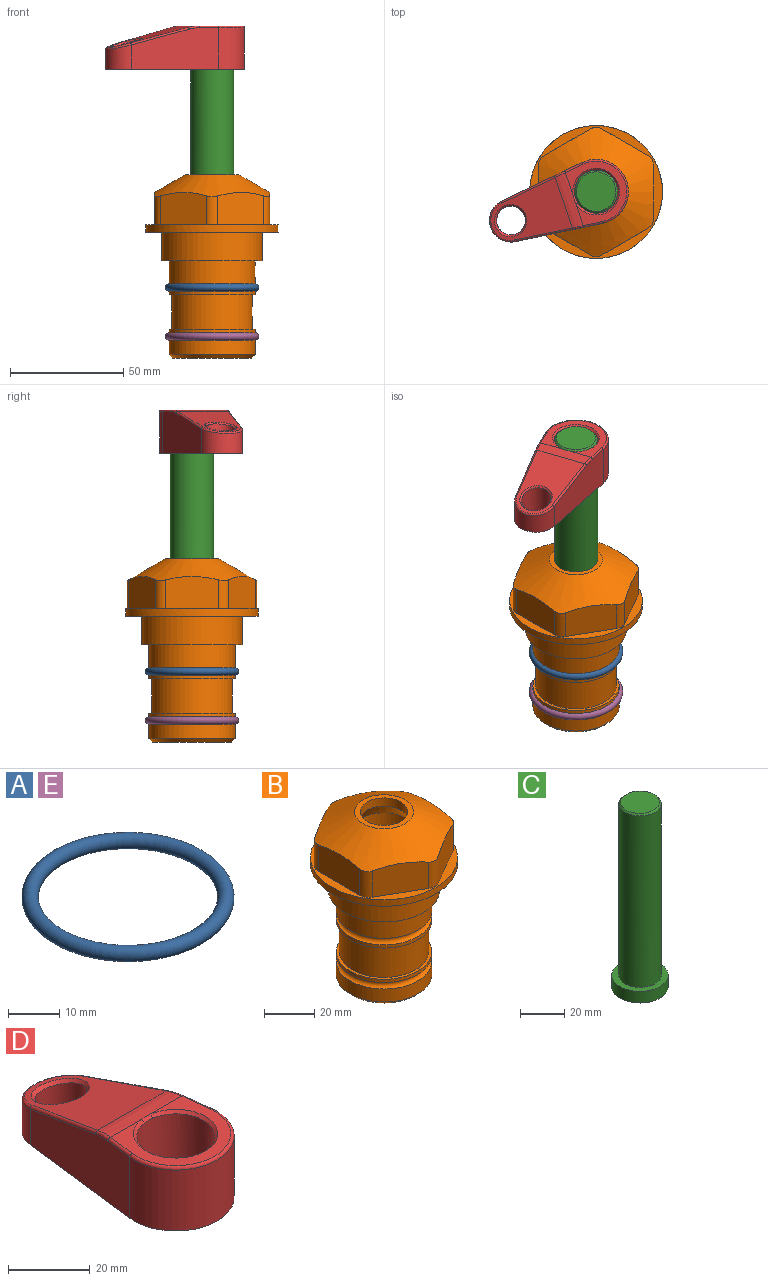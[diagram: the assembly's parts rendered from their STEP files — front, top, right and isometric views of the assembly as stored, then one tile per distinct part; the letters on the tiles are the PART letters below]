
ASSEMBLY  parts=5 mates=4
PART A: 1 faces, bbox 44.7x44.7x3.2 mm
  f0: torus R=19.05mm, axis (0,0,1), area 1193.9mm2
PART B: 36 faces, bbox 58.7x58.7x81 mm
  f0: cylinder r=17.78mm len=35.56mm, axis (0,0,1), area 1670.8mm2, adj f23,f24,f31
  f1: cylinder r=19.05mm len=38.1mm, axis (0,0,1), area 1191.9mm2, adj f26,f27,f30
  f2: plane 58.66x58.66mm, normal (0,0,-1), area 1150.6mm2, adj f3,f28
  f3: cylinder r=29.33mm len=58.66mm, axis (0,0,-1), area 585.1mm2, adj f2,f4
  f4: plane 58.66x58.66mm, normal (0,0,1), area 475.9mm2, adj f3,f5,f6,f7,f8,f9,f10,f11
  f5: plane 20.32x14.34mm, normal (-0.5,0.87,0), area 324.4mm2, adj f4,f15,f16,f17
  f6: plane 20.32x14.34mm, normal (0.5,0.87,0), area 324.4mm2, adj f4,f14,f15,f17
  f7: plane 23.48x14.34mm, normal (1,0,0), area 324.4mm2, adj f4,f13,f14,f17
  f8: plane 20.32x14.34mm, normal (0.5,-0.87,0), area 324.4mm2, adj f4,f12,f13,f17
  f9: plane 20.32x14.34mm, normal (-0.5,-0.87,0), area 324.4mm2, adj f4,f11,f12,f17
  f10: plane 23.48x14.34mm, normal (-1,0,0), area 324.4mm2, adj f4,f11,f16,f17
  f11: cylinder r=5.08mm len=12.85mm, axis (0,0,-1), area 67.2mm2, adj f4,f9,f10,f17
  f12: cylinder r=5.08mm len=12.85mm, axis (0,0,-1), area 67.2mm2, adj f4,f8,f9,f17
  f13: cylinder r=5.08mm len=12.85mm, axis (0,0,-1), area 67.2mm2, adj f4,f7,f8,f17
  f14: cylinder r=5.08mm len=12.85mm, axis (0,0,-1), area 67.2mm2, adj f4,f6,f7,f17
  f15: cylinder r=5.08mm len=12.85mm, axis (0,0,-1), area 67.2mm2, adj f4,f5,f6,f17
  f16: cylinder r=5.08mm len=12.85mm, axis (0,0,-1), area 67.2mm2, adj f4,f5,f10,f17
  f17: cone r=11.73mm half-angle=60deg, axis (0,0,-1), area 2071.8mm2, adj f5,f6,f7,f8,f9,f10,f11,f12
  f18: plane 23.46x23.46mm, normal (0,0,1), area 147.4mm2, adj f17,f35
  f19: plane 34.93x34.93mm, normal (0,0,-1), area 958mm2, adj f29
  f20: cylinder r=19.05mm len=38.1mm, axis (0,0,1), area 760.1mm2, adj f21,f29
  f21: torus R=19.05mm, axis (0,0,1), area 565.3mm2, adj f20,f22
  f22: cylinder r=19.05mm len=38.1mm, axis (0,0,1), area 190mm2, adj f21,f23
  f23: plane 38.1x38.1mm, normal (0,0,1), area 146.9mm2, adj f0,f22
  f24: plane 38.1x38.1mm, normal (0,0,-1), area 146.9mm2, adj f0,f25
  f25: cylinder r=19.05mm len=38.1mm, axis (0,0,1), area 190mm2, adj f24,f26
  f26: torus R=19.05mm, axis (0,0,1), area 565.3mm2, adj f1,f25
  f27: plane 44.45x44.45mm, normal (0,0,-1), area 411.7mm2, adj f1,f28
  f28: cylinder r=22.23mm len=44.45mm, axis (0,0,1), area 1773.5mm2, adj f2,f27
  f29: cone r=19.05mm half-angle=45deg, axis (0,0,1), area 257.5mm2, adj f19,f20
  f30: cylinder r=3.17mm len=6.75mm, axis (-1,0,0), area 128mm2, adj f1,f33
  f31: cylinder r=3.17mm len=6.35mm, axis (-1,0,0), area 102.5mm2, adj f0,f33
  f32: plane 25.4x25.4mm, normal (0,0,1), area 506.7mm2, adj f33
  f33: cylinder r=12.7mm len=66.42mm, axis (0,0,-1), area 5236.2mm2, adj f30,f31,f32,f34
  f34: cone r=9.53mm half-angle=30deg, axis (0,0,-1), area 443.4mm2, adj f33,f35
  f35: cylinder r=9.53mm len=19.05mm, axis (0,0,-1), area 240.9mm2, adj f18,f34
PART C: 6 faces, bbox 25.4x25.4x101.6 mm
  f0: plane 17.46x17.46mm, normal (0,0,1), area 239.5mm2, adj f5
  f1: plane 25.4x25.4mm, normal (0,0,-1), area 506.7mm2, adj f2
  f2: cylinder r=12.7mm len=25.4mm, axis (0,0,1), area 506.7mm2, adj f1,f3
  f3: plane 25.4x25.4mm, normal (0,0,1), area 221.7mm2, adj f2,f4
  f4: cylinder r=9.53mm len=94.46mm, axis (0,0,1), area 5653mm2, adj f3,f5
  f5: cone r=8.73mm half-angle=45deg, axis (0,0,-1), area 64.4mm2, adj f0,f4
PART D: 31 faces, bbox 31.7x65.5x19.8 mm
  f0: plane 39.12x18.26mm, normal (0.99,0.12,0), area 612.2mm2, adj f1,f4,f7,f11,f13,f15
  f1: cylinder r=9.53mm len=18.91mm, axis (0,0,-1), area 296.1mm2, adj f0,f2,f7,f17
  f2: plane 39.12x18.26mm, normal (-0.99,0.12,0), area 612.2mm2, adj f1,f4,f7,f12,f14,f16
  f3: cylinder r=6.35mm len=12.7mm, axis (0,0,-1), area 362.4mm2, adj f7,f18
  f4: cylinder r=14.29mm len=28.58mm, axis (0,0,-1), area 882.2mm2, adj f0,f2,f7,f10
  f5: cylinder r=9.53mm len=19.05mm, axis (0,0,-1), area 1092.6mm2, adj f7,f19,f20
  f6: plane 26.99x23.69mm, normal (0,0,1), area 216.2mm2, adj f9,f10,f11,f12,f19
  f7: plane 63.5x28.58mm, normal (0,0,-1), area 661.8mm2, adj f0,f1,f2,f3,f4,f5,f22,f23
  f8: plane 33.52x23.6mm, normal (0,0.26,0.97), area 486mm2, adj f9,f15,f16,f17,f18
  f9: cylinder r=19.05mm len=24.72mm, axis (1,0,0), area 120.4mm2, adj f6,f8,f13,f14,f20
  f10: torus R=13.49mm, axis (0,0,1), area 59mm2, adj f4,f6,f11,f12
  f11: cylinder r=0.79mm len=8.67mm, axis (0.12,-0.99,0), area 10.8mm2, adj f0,f6,f10,f13
  f12: cylinder r=0.79mm len=8.67mm, axis (0.12,0.99,0), area 10.8mm2, adj f2,f6,f10,f14
  f13: bspline ~4.95x1.42mm, area 6.1mm2, adj f0,f9,f11,f15
  f14: bspline ~4.95x1.42mm, area 6.1mm2, adj f2,f9,f12,f16
  f15: cylinder r=0.79mm len=25.95mm, axis (0.12,-0.96,0.26), area 32.9mm2, adj f0,f8,f13,f17
  f16: cylinder r=0.79mm len=25.95mm, axis (0.12,0.96,-0.26), area 32.9mm2, adj f2,f8,f14,f17
  f17: bspline ~18.91x8.38mm, area 30mm2, adj f1,f8,f15,f16
  f18: bspline ~14.29x14.29mm, area 48.3mm2, adj f3,f8
  f19: cone r=9.53mm half-angle=45deg, axis (0,0,1), area 66.5mm2, adj f5,f6,f20
  f20: bspline ~3.22x0.96mm, area 3.5mm2, adj f5,f9,f19
  f21: plane 2.75x2.72mm, normal (0,0,-1), area 2.9mm2, adj f23,f25,f28
  f22: plane 23.05x15.88mm, normal (-0.99,-0.12,0), area 323.6mm2, adj f7,f25,f26,f27,f28,f29
  f23: plane 23.05x15.88mm, normal (0.99,-0.12,0), area 323.6mm2, adj f7,f21,f25,f27,f28,f30
  f24: cylinder r=9.53mm len=10.69mm, axis (0,0,-1), area 114.7mm2, adj f7,f27,f29,f30
  f25: cylinder r=12.7mm len=20.59mm, axis (0,0,-1), area 381.1mm2, adj f7,f21,f22,f23,f26,f28
  f26: plane 2.75x2.72mm, normal (0,0,-1), area 2.9mm2, adj f22,f25,f28
  f27: plane 19.72x18.37mm, normal (0,-0.26,-0.97), area 291.8mm2, adj f22,f23,f24,f28,f29,f30
  f28: cylinder r=15.88mm len=19.92mm, axis (1,0,0), area 54.8mm2, adj f21,f22,f23,f25,f26,f27
  f29: cylinder r=1.59mm len=11mm, axis (0,0,-1), area 34.7mm2, adj f7,f22,f24,f27
  f30: cylinder r=1.59mm len=11mm, axis (0,0,-1), area 34.7mm2, adj f7,f23,f24,f27
PART E: same geometry as A
PLACE A at identity
PLACE B at identity fixed
PLACE C rot(axis=(0,0,1),108.7deg) t=(0,0,27.55)mm
PLACE D rot(axis=(0,0,1),108.7deg) t=(0,0,27.55)mm
PLACE E t=(0,0,-21.59)mm
MATE fastened B.f0 <-> E.f0  axis (0,0,1) through (0,0,-46.1)mm
MATE cylindrical C.f2 <-> B.f0  axis (0,0,-1) through (0,0,-10.55)mm
MATE fastened D.f4 <-> C.f2  axis (0,0,1) through (0,0,91.05)mm
MATE fastened A.f0 <-> B.f0  axis (0,0,1) through (0,0,-24.51)mm
